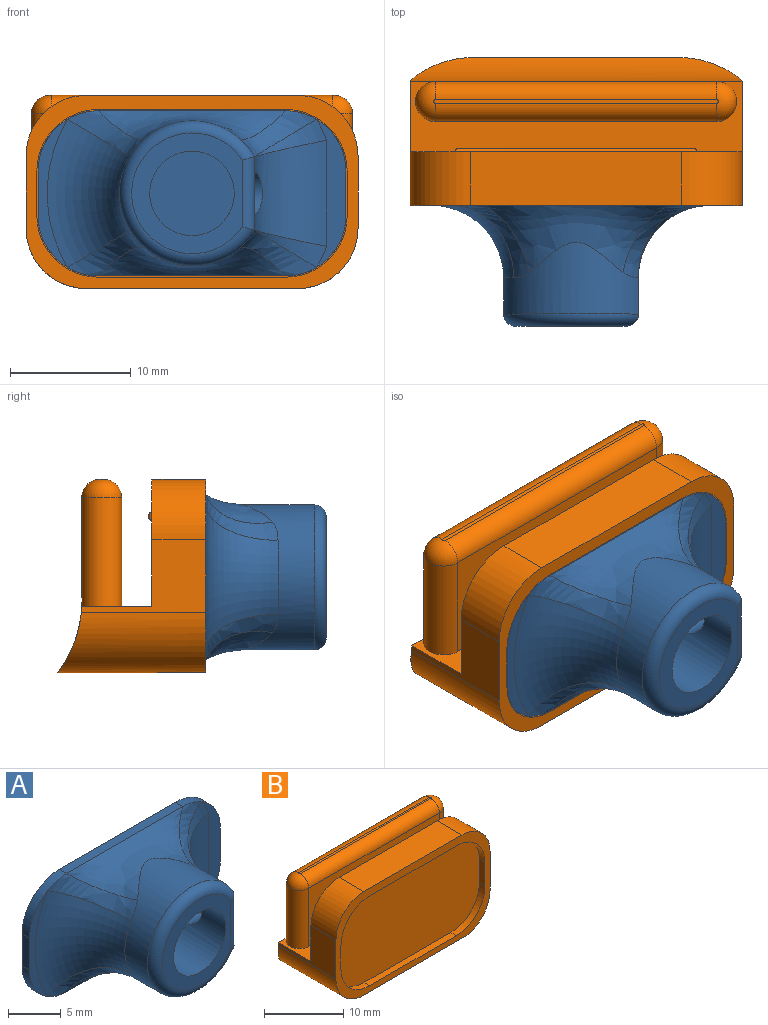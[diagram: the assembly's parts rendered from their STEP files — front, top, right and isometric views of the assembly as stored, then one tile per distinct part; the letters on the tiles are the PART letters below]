
ASSEMBLY  parts=2 mates=1
PART A: 29 faces, bbox 33.4x11.9x18.6 mm
  f0: cylinder r=3.5mm len=10mm, axis (0,-1,0), area 210mm2, adj f13,f15,f28
  f1: plane 12.27x2.44mm, normal (0,-1,0), area 9.8mm2, adj f7,f8,f9,f16
  f2: cylinder r=6mm len=12mm, axis (0,1,0), area 126.6mm2, adj f14,f16,f17,f18,f19,f20,f21,f22
  f3: plane 12.27x2.44mm, normal (0,-1,0), area 14.7mm2, adj f4,f5,f11,f23,f24,f25
  f4: plane 3.68x1mm, normal (1,0,0), area 3.7mm2, adj f3,f5,f11,f12
  f5: cylinder r=5mm len=5mm, axis (0,1,0), area 7.9mm2, adj f3,f4,f6,f12,f22
  f6: plane 16.13x1.62mm, normal (0,0,1), area 15.5mm2, adj f5,f7,f12,f20
  f7: cylinder r=5mm len=5mm, axis (0,1,0), area 7.9mm2, adj f1,f6,f8,f12,f18
  f8: plane 3.68x1mm, normal (-1,0,0), area 3.7mm2, adj f1,f7,f9,f12
  f9: cylinder r=5mm len=5mm, axis (0,1,0), area 7.9mm2, adj f1,f8,f10,f12,f17
  f10: plane 16.13x1.62mm, normal (0,0,-1), area 15.5mm2, adj f9,f11,f12,f19
  f11: cylinder r=5mm len=5mm, axis (0,1,0), area 7.9mm2, adj f3,f4,f10,f12,f21
  f12: plane 25.5x13.68mm, normal (0,1,0), area 327.5mm2, adj f4,f5,f6,f7,f8,f9,f10,f11
  f13: plane 10x9.17mm, normal (0,-1,0), area 36.9mm2, adj f0,f26,f27
  f14: plane 6.09x3mm, normal (1,0,0), area 16.8mm2, adj f2,f15,f25,f27
  f15: cylinder r=1.75mm len=3.5mm, axis (1,0,0), area 22.6mm2, adj f0,f14,f25
  f16: torus R=12mm, axis (0,-1,0), area 82.8mm2, adj f1,f2,f17,f18
  f17: bspline ~8.12x6.7mm, area 14.7mm2, adj f2,f9,f16,f19
  f18: bspline ~7.18x6.33mm, area 14.7mm2, adj f2,f7,f16,f20
  f19: bspline ~17.28x5.88mm, area 54.4mm2, adj f2,f10,f17,f21
  f20: bspline ~17.28x5.88mm, area 54.4mm2, adj f2,f6,f18,f22
  f21: bspline ~7.18x6.33mm, area 14.7mm2, adj f2,f11,f19,f23
  f22: bspline ~8.12x6.7mm, area 14.7mm2, adj f2,f5,f20,f24
  f23: torus R=12mm, axis (0,-1,0), area 6.5mm2, adj f2,f3,f21,f25
  f24: torus R=12mm, axis (0,-1,0), area 6.5mm2, adj f2,f3,f22,f25
  f25: cylinder r=6mm len=8.78mm, axis (0,0,1), area 61.7mm2, adj f3,f14,f15,f23,f24
  f26: torus R=5mm, axis (0,-1,0), area 45.7mm2, adj f2,f13,f27
  f27: cylinder r=1mm len=6.09mm, axis (0,0,1), area 9.1mm2, adj f13,f14,f26
  f28: plane 7x7mm, normal (0,-1,0), area 38.5mm2, adj f0
PART B: 37 faces, bbox 27.5x12.3x16 mm
  f0: plane 27.5x15.95mm, normal (0,-1,0), area 83.2mm2, adj f4,f21,f22,f23,f24,f25,f26,f27
  f1: cylinder r=5mm len=18.87mm, axis (-1,0,0), area 12.5mm2, adj f3,f23,f24,f26
  f2: plane 27.5x5.8mm, normal (0,0,1), area 74.1mm2, adj f5,f6,f7,f8,f10,f21,f22
  f3: plane 17.5x8.07mm, normal (0,0,-1), area 141.2mm2, adj f1,f6,f24,f26
  f4: plane 17.5x4.45mm, normal (0,0,1), area 77.9mm2, adj f0,f5,f25,f27
  f5: plane 27.5x10.5mm, normal (0,1,0), area 264.5mm2, adj f2,f4,f17,f18,f19,f20,f21,f22
  f6: cylinder r=10mm len=27.5mm, axis (-1,0,0), area 175.4mm2, adj f2,f3,f7,f8,f9,f21,f22,f24
  f7: cylinder r=1.65mm len=9mm, axis (0,0,-1), area 46.5mm2, adj f2,f6,f9,f10,f14
  f8: cylinder r=1.65mm len=9mm, axis (0,0,-1), area 46.5mm2, adj f2,f6,f9,f10,f13
  f9: plane 23.3x7.96mm, normal (0,1,0), area 185.6mm2, adj f6,f7,f8,f12
  f10: plane 23.3x9mm, normal (0,-1,0), area 209.7mm2, adj f2,f7,f8,f15
  f11: plane 23.6x0.3mm, normal (0,0,1), area 7.1mm2, adj f12,f13,f14,f15
  f12: cylinder r=1.5mm len=23.3mm, axis (1,0,0), area 54.9mm2, adj f9,f11,f13,f14
  f13: torus R=0.15mm, axis (0,0,1), area 8.2mm2, adj f8,f11,f12,f15
  f14: torus R=0.15mm, axis (0,0,1), area 8.2mm2, adj f7,f11,f12,f15
  f15: cylinder r=1.5mm len=23.3mm, axis (-1,0,0), area 54.9mm2, adj f10,f11,f13,f14
  f16: plane 19.5x0.18mm, normal (0,1,0), area 3.5mm2, adj f17,f18,f19,f20
  f17: cylinder r=0.25mm len=20mm, axis (-1,0,0), area 7.8mm2, adj f5,f16,f18,f19
  f18: cylinder r=0.25mm len=0.68mm, axis (0,0,1), area 0.2mm2, adj f5,f16,f17,f20
  f19: cylinder r=0.25mm len=0.68mm, axis (0,0,-1), area 0.2mm2, adj f5,f16,f17,f20
  f20: cylinder r=0.25mm len=20mm, axis (1,0,0), area 7.8mm2, adj f5,f16,f18,f19
  f21: plane 10.29x6mm, normal (-1,0,0), area 29.6mm2, adj f0,f2,f5,f6,f26,f27
  f22: plane 10.29x6mm, normal (1,0,0), area 29.6mm2, adj f0,f2,f5,f6,f24,f25
  f23: plane 18.87x3.5mm, normal (0,0,-1), area 66mm2, adj f0,f1,f24,f26
  f24: cylinder r=5mm len=12.25mm, axis (0,-1,0), area 86.3mm2, adj f0,f1,f3,f6,f22,f23
  f25: cylinder r=5mm len=5mm, axis (0,1,0), area 35mm2, adj f0,f4,f5,f22
  f26: cylinder r=5mm len=12.25mm, axis (0,1,0), area 86.3mm2, adj f0,f1,f3,f6,f21,f23
  f27: cylinder r=5mm len=5mm, axis (0,-1,0), area 35mm2, adj f0,f4,f5,f21
  f28: plane 3.68x1mm, normal (1,0,0), area 3.7mm2, adj f0,f29,f35,f36
  f29: cylinder r=5.1mm len=5.1mm, axis (0,-1,0), area 8mm2, adj f0,f28,f30,f36
  f30: plane 15.5x1mm, normal (0,0,1), area 15.5mm2, adj f0,f29,f31,f36
  f31: cylinder r=5.1mm len=5.1mm, axis (0,-1,0), area 8mm2, adj f0,f30,f32,f36
  f32: plane 3.68x1mm, normal (-1,0,0), area 3.7mm2, adj f0,f31,f33,f36
  f33: cylinder r=5.1mm len=5.1mm, axis (0,-1,0), area 8mm2, adj f0,f32,f34,f36
  f34: plane 15.5x1mm, normal (0,0,-1), area 15.5mm2, adj f0,f33,f35,f36
  f35: cylinder r=5.1mm len=5.1mm, axis (0,-1,0), area 8mm2, adj f0,f28,f34,f36
  f36: plane 25.7x13.88mm, normal (0,-1,0), area 334.5mm2, adj f28,f29,f30,f31,f32,f33,f34,f35
PLACE A t=(0,-2.5,0)mm
PLACE B at identity
MATE fastened A.f0 <-> B.f36  axis (0,1,0) through (0,-7.6,7.89)mm
